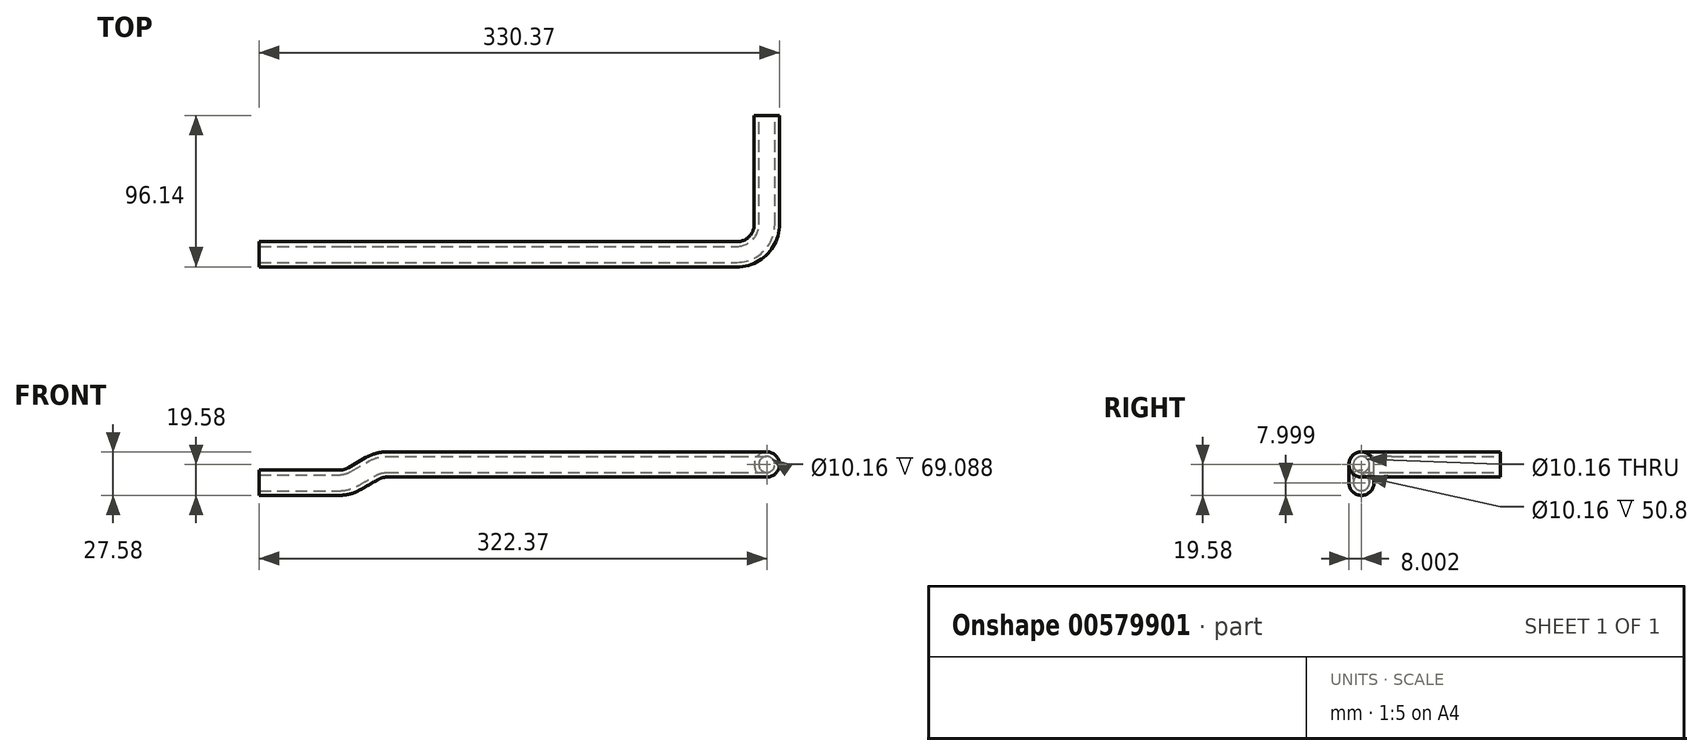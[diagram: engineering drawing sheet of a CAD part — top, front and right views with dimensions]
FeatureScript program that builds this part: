
annotation { "Feature Type Name" : "Feature", "Feature Type Description" : "" }
export const myFeature = defineFeature(function(context is Context, id is Id, definition is map)
    precondition{}
    {
        {
            var Q0;
            Q0=qCreatedBy(makeId("Front.planeOp"),FACE);
            var sketch = newSketch(context, id + "F0", { "sketchPlane" : qUnion([Q0])});
            skCircle(sketch, "E0", {"center": v(0, 0) * mm, "radius": 8 * mm});
            skCircle(sketch, "E1", {"center": v(0, 0) * mm, "radius": 5.08 * mm});
            skSolve(sketch);
        }
        {
            var Q0;
            Q0=qSketchRegion(id+"F0",true);
            extrude(context, id + "F1", {"entities" : qUnion([Q0]), "depth" : 69.1 * mm, "offsetDistance" : 25.4 * mm});
        }
        {
            var Q0;
            Q0=makeQuery(id+"F1.opExtrude","CAP_FACE",FACE,{"disambiguationData":[OSD([sQuery(id+"F0.wireOp",EDGE,"E0"),sQuery(id+"F0.wireOp",EDGE,"E1")])],"isStart":false});
            var sketch = newSketch(context, id + "F2", { "sketchPlane" : qUnion([Q0])});
            skCircle(sketch, "E2", {"center": v(0, 0) * mm, "radius": 5.08 * mm});
            skCircle(sketch, "E3", {"center": v(0, 0) * mm, "radius": 8 * mm});
            skLineSegment(sketch, "E4", {"start": v(-19.05, 14.22) * mm, "end": v(-19.05, -8.33) * mm});
            skSolve(sketch);
        }
        {
            var Q0;
            Q0=qSketchRegion(id+"F2",true);
            var Q1;
            Q1=sQuery(id+"F2.wireOp",EDGE,"E4");
            revolve(context, id + "F3", {"operationType" : NewBodyOperationType.ADD, "entities" : qUnion([Q0]), "axis" : qUnion([Q1]), "revolveType" : RevolveType.ONE_DIRECTION, "angle" : 90 * degree});
        }
        {
            var Q0;
            Q0=makeQuery(id+"F3.opRevolve","CAP_FACE",FACE,{"disambiguationData":[OSD([sQuery(id+"F2.wireOp",EDGE,"E2"),sQuery(id+"F2.wireOp",EDGE,"E3")])],"isStart":false});
            var sketch = newSketch(context, id + "F4", { "sketchPlane" : qUnion([Q0])});
            skCircle(sketch, "E5", {"center": v(88.14, 0) * mm, "radius": 8 * mm});
            skCircle(sketch, "E6", {"center": v(88.14, 0) * mm, "radius": 5.08 * mm});
            skSolve(sketch);
        }
        {
            var Q0;
            Q0=qSketchRegion(id+"F4",true);
            extrude(context, id + "F5", {"entities" : qUnion([Q0]), "operationType" : NewBodyOperationType.ADD, "depth" : 222.25 * mm, "offsetDistance" : 25.4 * mm});
        }
        {
            var Q0;
            Q0=makeQuery(id+"F5.opExtrude","CAP_FACE",FACE,{"disambiguationData":[OSD([sQuery(id+"F4.wireOp",EDGE,"E5"),sQuery(id+"F4.wireOp",EDGE,"E6")])],"isStart":false});
            var sketch = newSketch(context, id + "F6", { "sketchPlane" : qUnion([Q0])});
            skCircle(sketch, "E7", {"center": v(88.14, 0) * mm, "radius": 8 * mm});
            skCircle(sketch, "E8", {"center": v(88.14, 0) * mm, "radius": 5.08 * mm});
            skLineSegment(sketch, "E9", {"start": v(78.18, -19.05) * mm, "end": v(100.27, -19.05) * mm});
            skSolve(sketch);
        }
        {
            var Q0;
            Q0=qSketchRegion(id+"F6",true);
            var Q1;
            Q1=sQuery(id+"F6.wireOp",EDGE,"E9");
            revolve(context, id + "F7", {"operationType" : NewBodyOperationType.ADD, "entities" : qUnion([Q0]), "axis" : qUnion([Q1]), "revolveType" : RevolveType.ONE_DIRECTION, "angle" : 30 * degree});
        }
        {
            var Q0;
            Q0=makeQuery(id+"F7.opRevolve","CAP_FACE",FACE,{"disambiguationData":[OSD([sQuery(id+"F6.wireOp",EDGE,"E7"),sQuery(id+"F6.wireOp",EDGE,"E8")])],"isStart":false});
            var sketch = newSketch(context, id + "F8", { "sketchPlane" : qUnion([Q0])});
            skCircle(sketch, "E10", {"center": v(88.14, 123.2) * mm, "radius": 8 * mm});
            skCircle(sketch, "E11", {"center": v(88.14, 123.2) * mm, "radius": 5.08 * mm});
            skSolve(sketch);
        }
        {
            var Q0;
            Q0=qSketchRegion(id+"F8",true);
            extrude(context, id + "F9", {"entities" : qUnion([Q0]), "operationType" : NewBodyOperationType.ADD, "depth" : 12.95 * mm, "offsetDistance" : 25.4 * mm});
        }
        {
            var Q0;
            Q0=makeQuery(id+"F9.opExtrude","CAP_FACE",FACE,{"disambiguationData":[OSD([sQuery(id+"F8.wireOp",EDGE,"E10"),sQuery(id+"F8.wireOp",EDGE,"E11")])],"isStart":false});
            var sketch = newSketch(context, id + "F10", { "sketchPlane" : qUnion([Q0])});
            skCircle(sketch, "E12", {"center": v(88.14, 123.2) * mm, "radius": 8 * mm});
            skCircle(sketch, "E13", {"center": v(88.14, 123.2) * mm, "radius": 5.08 * mm});
            skLineSegment(sketch, "E14", {"start": v(76.68, 142.25) * mm, "end": v(99.87, 142.25) * mm});
            skSolve(sketch);
        }
        {
            var Q0;
            Q0=qSketchRegion(id+"F10",true);
            var Q1;
            Q1=sQuery(id+"F10.wireOp",EDGE,"E14");
            revolve(context, id + "F11", {"operationType" : NewBodyOperationType.ADD, "entities" : qUnion([Q0]), "axis" : qUnion([Q1]), "revolveType" : RevolveType.ONE_DIRECTION, "oppositeDirection" : true, "angle" : 30 * degree});
        }
        {
            var Q0;
            Q0=makeQuery(id+"F11.opRevolve","CAP_FACE",FACE,{"disambiguationData":[OSD([sQuery(id+"F10.wireOp",EDGE,"E12"),sQuery(id+"F10.wireOp",EDGE,"E13")])],"isStart":false});
            var sketch = newSketch(context, id + "F12", { "sketchPlane" : qUnion([Q0])});
            skCircle(sketch, "E15", {"center": v(88.14, -11.58) * mm, "radius": 8 * mm});
            skCircle(sketch, "E16", {"center": v(88.14, -11.58) * mm, "radius": 5.08 * mm});
            skSolve(sketch);
        }
        {
            var Q0;
            Q0=qSketchRegion(id+"F12",true);
            extrude(context, id + "F13", {"entities" : qUnion([Q0]), "operationType" : NewBodyOperationType.ADD, "depth" : 50.8 * mm, "offsetDistance" : 25.4 * mm});
        }
    });
